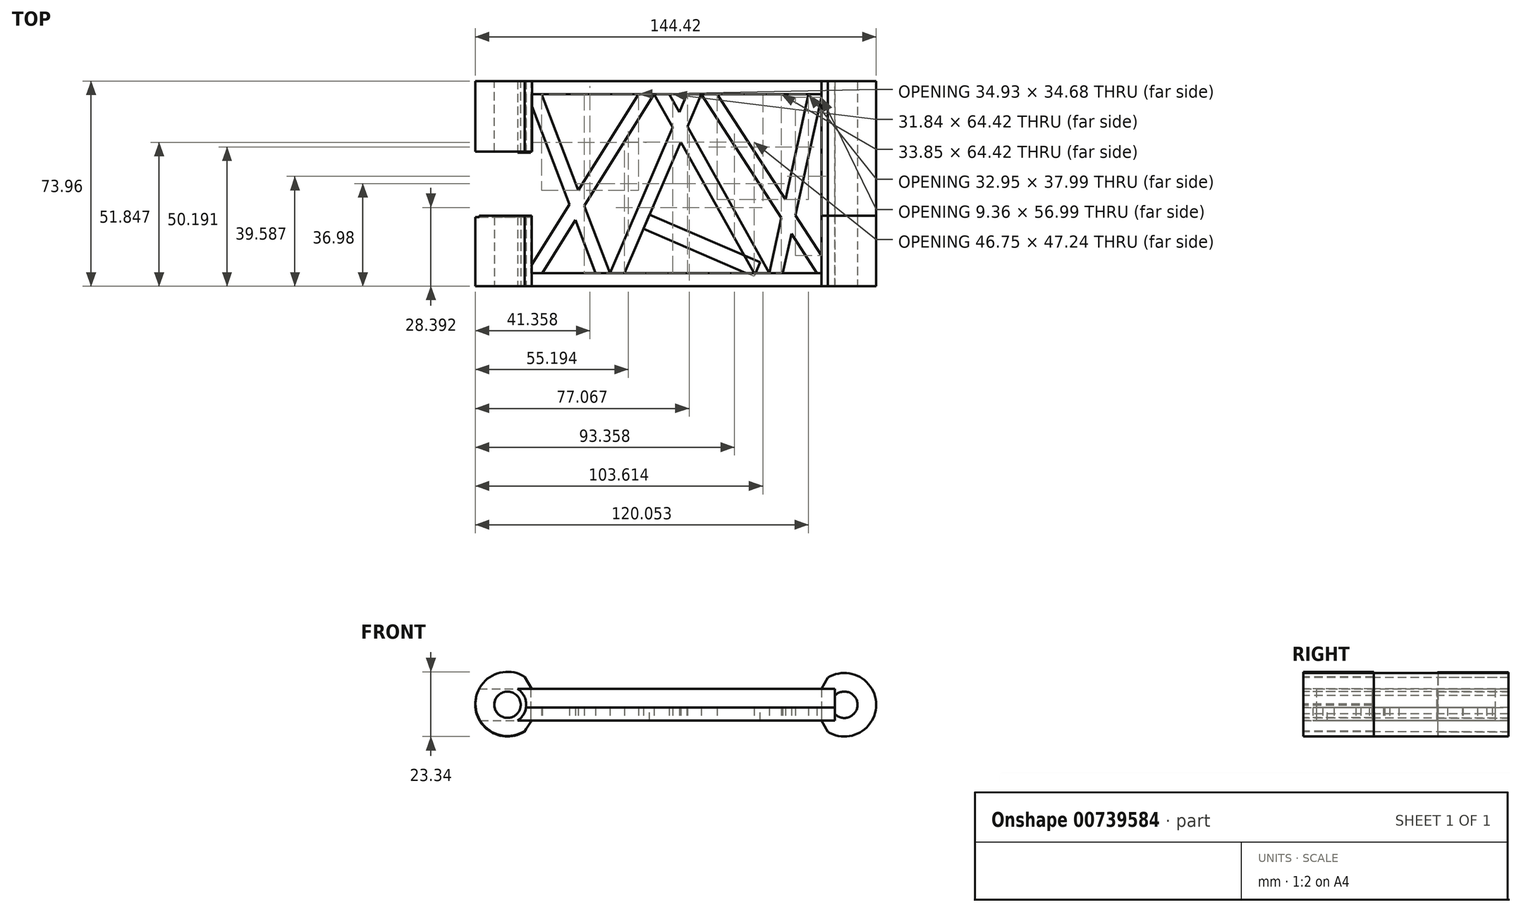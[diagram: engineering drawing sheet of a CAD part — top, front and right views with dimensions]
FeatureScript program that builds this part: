
annotation { "Feature Type Name" : "Feature", "Feature Type Description" : "" }
export const myFeature = defineFeature(function(context is Context, id is Id, definition is map)
    precondition{}
    {
        {
            var Q0;
            Q0=qCreatedBy(makeId("Top.planeOp"),FACE);
            var sketch = newSketch(context, id + "F0", { "sketchPlane" : qUnion([Q0])});
            skLineSegment(sketch, "E0", {"start": v(-109.82, 45.91) * mm, "end": v(-109.82, -28.05) * mm});
            skLineSegment(sketch, "E1", {"start": v(-109.82, -28.05) * mm, "end": v(4.48, -28.05) * mm});
            skLineSegment(sketch, "E2", {"start": v(4.48, -28.05) * mm, "end": v(4.48, 45.91) * mm});
            skLineSegment(sketch, "E3", {"start": v(4.48, 45.91) * mm, "end": v(-109.82, 45.91) * mm});
            skLineSegment(sketch, "E4.0", {"start": v(-105.05, 41.14) * mm, "end": v(-105.05, -23.28) * mm});
            skLineSegment(sketch, "E4.1", {"start": v(-0.3, 41.14) * mm, "end": v(-105.05, 41.14) * mm});
            skLineSegment(sketch, "E4.2", {"start": v(-0.3, -23.28) * mm, "end": v(-0.3, 41.14) * mm});
            skLineSegment(sketch, "E4.3", {"start": v(-105.05, -23.28) * mm, "end": v(-0.3, -23.28) * mm});
            skLineSegment(sketch, "E5", {"start": v(-42.79, -23.28) * mm, "end": v(-36.04, -23.28) * mm});
            skLineSegment(sketch, "E6", {"start": v(-10.41, 41.14) * mm, "end": v(-5.27, 41.14) * mm});
            skLineSegment(sketch, "E7", {"start": v(1.6, 41.14) * mm, "end": v(-0.3, 41.76) * mm});
            skLineSegment(sketch, "E8", {"start": v(-43.58, 41.14) * mm, "end": v(-37.89, 41.14) * mm});
            skLineSegment(sketch, "E9", {"start": v(-9.59, 41.14) * mm, "end": v(-0.3, 41.14) * mm});
            skLineSegment(sketch, "E10", {"start": v(-105.05, -20.98) * mm, "end": v(-66.2, 41.14) * mm});
            skLineSegment(sketch, "E11", {"start": v(-66.2, 41.14) * mm, "end": v(-60.57, 41.14) * mm});
            skLineSegment(sketch, "E12", {"start": v(-60.57, 41.14) * mm, "end": v(-100.85, -23.28) * mm});
            skLineSegment(sketch, "E13", {"start": v(-60.57, 41.14) * mm, "end": v(-24.59, -23.28) * mm});
            skLineSegment(sketch, "E14", {"start": v(-24.59, -23.28) * mm, "end": v(-19.12, -23.28) * mm});
            skLineSegment(sketch, "E15", {"start": v(-19.12, -23.28) * mm, "end": v(-55.1, 41.14) * mm});
            skLineSegment(sketch, "E16", {"start": v(-55.1, 41.14) * mm, "end": v(-60.57, 41.14) * mm});
            skLineSegment(sketch, "E17", {"start": v(-19.12, -23.28) * mm, "end": v(-4.94, 41.14) * mm});
            skLineSegment(sketch, "E18", {"start": v(-4.94, 41.14) * mm, "end": v(-0.3, 41.14) * mm});
            skLineSegment(sketch, "E19", {"start": v(-0.3, 41.14) * mm, "end": v(-0.3, 40.03) * mm});
            skLineSegment(sketch, "E20", {"start": v(-0.3, 40.03) * mm, "end": v(-14.23, -23.28) * mm});
            skLineSegment(sketch, "E21", {"start": v(-1.9, -23.28) * mm, "end": v(-43.58, 41.14) * mm});
            skLineSegment(sketch, "E22", {"start": v(-37.89, 41.14) * mm, "end": v(-0.3, -16.96) * mm});
            skLineSegment(sketch, "E23", {"start": v(-0.3, -16.96) * mm, "end": v(-0.3, -23.28) * mm});
            skLineSegment(sketch, "E24", {"start": v(-43.58, 41.14) * mm, "end": v(-71.34, -23.28) * mm});
            skLineSegment(sketch, "E25", {"start": v(-71.34, -23.28) * mm, "end": v(-76.54, -23.28) * mm});
            skLineSegment(sketch, "E26", {"start": v(-76.54, -23.28) * mm, "end": v(-48.78, 41.14) * mm});
            skLineSegment(sketch, "E27", {"start": v(-48.78, 41.14) * mm, "end": v(-43.58, 41.14) * mm});
            skLineSegment(sketch, "E28", {"start": v(-76.54, -23.28) * mm, "end": v(-101.14, 41.14) * mm});
            skLineSegment(sketch, "E29", {"start": v(-101.14, 41.14) * mm, "end": v(-105.05, 41.14) * mm});
            skLineSegment(sketch, "E30", {"start": v(-105.05, 37.99) * mm, "end": v(-81.65, -23.28) * mm});
            skLineSegment(sketch, "E31", {"start": v(-81.65, -23.28) * mm, "end": v(-76.54, -23.28) * mm});
            skSolve(sketch);
        }
        {
            var Q0;
            {var subQ5=sQuery(id+"F0.wireOp",EDGE,"E4.0");var subQ7=sQuery(id+"F0.wireOp",EDGE,"E30");var subQ8=makeQuery(id+"F0.imprint","INTERSECT",VERTEX,{"derivedFrom":[subQ5,subQ7]});Q0=makeQuery(id+"F0.imprint","IMPRINT",FACE,{"disambiguationData":[TD([[makeQuery(id+"F0.imprint","IMPRINT",EDGE,{"disambiguationData":[TD([[subQ8,1.0]])],"derivedFrom":subQ5}),1.0]])]});}
            var Q1;
            {var subQ3=sQuery(id+"F0.wireOp",EDGE,"E4.3");var subQ6=sQuery(id+"F0.wireOp",EDGE,"E4.0");var subQ9=makeQuery(id+"F0.imprint","INTERSECT",VERTEX,{"derivedFrom":[subQ6,subQ3]});Q1=makeQuery(id+"F0.imprint","IMPRINT",FACE,{"disambiguationData":[TD([[makeQuery(id+"F0.imprint","IMPRINT",EDGE,{"disambiguationData":[TD([[subQ9,1.0]])],"derivedFrom":subQ6}),1.0]])]});}
            var Q2;
            {var subQ0=sQuery(id+"F0.wireOp",EDGE,"E28");var subQ1=sQuery(id+"F0.wireOp",EDGE,"E10");var subQ2=makeQuery(id+"F0.imprint","INTERSECT",VERTEX,{"derivedFrom":[subQ1,subQ0]});Q2=makeQuery(id+"F0.imprint","IMPRINT",FACE,{"disambiguationData":[TD([[makeQuery(id+"F0.imprint","IMPRINT",EDGE,{"disambiguationData":[TD([[subQ2,1.0]])],"derivedFrom":subQ1}),-1.0]])]});}
            var Q3;
            {var subQ3=sQuery(id+"F0.wireOp",EDGE,"E30");var subQ5=sQuery(id+"F0.wireOp",EDGE,"E12");var subQ7=makeQuery(id+"F0.imprint","INTERSECT",VERTEX,{"derivedFrom":[subQ5,subQ3]});Q3=makeQuery(id+"F0.imprint","IMPRINT",FACE,{"disambiguationData":[TD([[makeQuery(id+"F0.imprint","IMPRINT",EDGE,{"disambiguationData":[TD([[subQ7,1.0]])],"derivedFrom":subQ5}),1.0]])]});}
            var Q4;
            {var subQ0=sQuery(id+"F0.wireOp",EDGE,"E10");var subQ1=sQuery(id+"F0.wireOp",EDGE,"E4.1");var subQ2=makeQuery(id+"F0.imprint","INTERSECT",VERTEX,{"derivedFrom":[subQ1,subQ0]});Q4=makeQuery(id+"F0.imprint","IMPRINT",FACE,{"disambiguationData":[TD([[makeQuery(id+"F0.imprint","IMPRINT",EDGE,{"disambiguationData":[TD([[subQ2,1.0]])],"derivedFrom":subQ0}),-1.0]])]});}
            var Q5;
            Q5=makeQuery(id+"F0.imprint","IMPRINT",FACE,{"disambiguationData":[TD([[makeQuery(id+"F0.imprint","IMPRINT",EDGE,{"derivedFrom":sQuery(id+"F0.wireOp",EDGE,"E0")}),1.0]])]});
            var Q6;
            {var subQ0=sQuery(id+"F0.wireOp",EDGE,"E24");var subQ5=sQuery(id+"F0.wireOp",EDGE,"E13");var subQ6=makeQuery(id+"F0.imprint","INTERSECT",VERTEX,{"derivedFrom":[subQ5,subQ0]});Q6=makeQuery(id+"F0.imprint","IMPRINT",FACE,{"disambiguationData":[TD([[makeQuery(id+"F0.imprint","IMPRINT",EDGE,{"disambiguationData":[TD([[subQ6,1.0]])],"derivedFrom":subQ5}),-1.0]])]});}
            var Q7;
            {var subQ0=sQuery(id+"F0.wireOp",EDGE,"E24");var subQ1=sQuery(id+"F0.wireOp",EDGE,"E13");var subQ2=makeQuery(id+"F0.imprint","INTERSECT",VERTEX,{"derivedFrom":[subQ1,subQ0]});Q7=makeQuery(id+"F0.imprint","IMPRINT",FACE,{"disambiguationData":[TD([[makeQuery(id+"F0.imprint","IMPRINT",EDGE,{"disambiguationData":[TD([[subQ2,1.0]])],"derivedFrom":subQ1}),1.0]])]});}
            var Q8;
            {var subQ3=sQuery(id+"F0.wireOp",EDGE,"E13");var subQ5=sQuery(id+"F0.wireOp",EDGE,"E24");var subQ7=makeQuery(id+"F0.imprint","INTERSECT",VERTEX,{"derivedFrom":[subQ3,subQ5]});Q8=makeQuery(id+"F0.imprint","IMPRINT",FACE,{"disambiguationData":[TD([[makeQuery(id+"F0.imprint","IMPRINT",EDGE,{"disambiguationData":[TD([[subQ7,-1.0]])],"derivedFrom":subQ3}),1.0]])]});}
            var Q9;
            {var subQ0=sQuery(id+"F0.wireOp",EDGE,"E26");var subQ5=sQuery(id+"F0.wireOp",EDGE,"E15");var subQ7=makeQuery(id+"F0.imprint","INTERSECT",VERTEX,{"derivedFrom":[subQ5,subQ0]});Q9=makeQuery(id+"F0.imprint","IMPRINT",FACE,{"disambiguationData":[TD([[makeQuery(id+"F0.imprint","IMPRINT",EDGE,{"disambiguationData":[TD([[subQ7,1.0]])],"derivedFrom":subQ5}),-1.0]])]});}
            var Q10;
            {var subQ3=sQuery(id+"F0.wireOp",EDGE,"E15");var subQ5=sQuery(id+"F0.wireOp",EDGE,"E26");var subQ6=makeQuery(id+"F0.imprint","INTERSECT",VERTEX,{"derivedFrom":[subQ3,subQ5]});Q10=makeQuery(id+"F0.imprint","IMPRINT",FACE,{"disambiguationData":[TD([[makeQuery(id+"F0.imprint","IMPRINT",EDGE,{"disambiguationData":[TD([[subQ6,-1.0]])],"derivedFrom":subQ3}),1.0]])]});}
            var Q11;
            {var subQ0=sQuery(id+"F0.wireOp",EDGE,"E22");var subQ5=sQuery(id+"F0.wireOp",EDGE,"E17");var subQ6=makeQuery(id+"F0.imprint","INTERSECT",VERTEX,{"derivedFrom":[subQ5,subQ0]});Q11=makeQuery(id+"F0.imprint","IMPRINT",FACE,{"disambiguationData":[TD([[makeQuery(id+"F0.imprint","IMPRINT",EDGE,{"disambiguationData":[TD([[subQ6,1.0]])],"derivedFrom":subQ5}),1.0]])]});}
            var Q12;
            {var subQ0=sQuery(id+"F0.wireOp",EDGE,"E22");var subQ1=sQuery(id+"F0.wireOp",EDGE,"E17");var subQ2=makeQuery(id+"F0.imprint","INTERSECT",VERTEX,{"derivedFrom":[subQ1,subQ0]});Q12=makeQuery(id+"F0.imprint","IMPRINT",FACE,{"disambiguationData":[TD([[makeQuery(id+"F0.imprint","IMPRINT",EDGE,{"disambiguationData":[TD([[subQ2,1.0]])],"derivedFrom":subQ1}),-1.0]])]});}
            var Q13;
            {var subQ3=sQuery(id+"F0.wireOp",EDGE,"E20");var subQ5=sQuery(id+"F0.wireOp",EDGE,"E21");var subQ7=makeQuery(id+"F0.imprint","INTERSECT",VERTEX,{"derivedFrom":[subQ3,subQ5]});Q13=makeQuery(id+"F0.imprint","IMPRINT",FACE,{"disambiguationData":[TD([[makeQuery(id+"F0.imprint","IMPRINT",EDGE,{"disambiguationData":[TD([[subQ7,-1.0]])],"derivedFrom":subQ3}),-1.0]])]});}
            var Q14;
            {var subQ5=sQuery(id+"F0.wireOp",EDGE,"E4.2");var subQ7=sQuery(id+"F0.wireOp",EDGE,"E22");var subQ9=makeQuery(id+"F0.imprint","INTERSECT",VERTEX,{"derivedFrom":[subQ5,subQ7]});Q14=makeQuery(id+"F0.imprint","IMPRINT",FACE,{"disambiguationData":[TD([[makeQuery(id+"F0.imprint","IMPRINT",EDGE,{"disambiguationData":[TD([[subQ9,1.0]])],"derivedFrom":subQ5}),1.0]])]});}
            var Q15;
            {var subQ1=sQuery(id+"F0.wireOp",EDGE,"E4.2");var subQ7=sQuery(id+"F0.wireOp",EDGE,"E4.1");var subQ9=makeQuery(id+"F0.imprint","INTERSECT",VERTEX,{"derivedFrom":[subQ7,subQ1]});Q15=makeQuery(id+"F0.imprint","IMPRINT",FACE,{"disambiguationData":[TD([[makeQuery(id+"F0.imprint","IMPRINT",EDGE,{"disambiguationData":[TD([[subQ9,-1.0]])],"derivedFrom":subQ7}),1.0]])]});}
            extrude(context, id + "F1", {"entities" : qUnion([Q0, Q1, Q2, Q3, Q4, Q5, Q6, Q7, Q8, Q9, Q10, Q11, Q12, Q13, Q14, Q15]), "depth" : 4.78 * mm, "offsetDistance" : 25.4 * mm});
        }
        {
            var Q0;
            Q0=makeQuery(id+"F0.imprint","IMPRINT",FACE,{"disambiguationData":[TD([[makeQuery(id+"F0.imprint","IMPRINT",EDGE,{"derivedFrom":sQuery(id+"F0.wireOp",EDGE,"E0")}),1.0]])]});
            extrude(context, id + "F2", {"entities" : qUnion([Q0]), "depth" : 11.43 * mm, "offsetDistance" : 25.4 * mm});
        }
        {
            var Q0;
            Q0=makeQuery(id+"F2.opExtrude","SWEPT_FACE",FACE,{"disambiguationData":[OSD([sQuery(id+"F0.wireOp",EDGE,"E1")])]});
            var sketch = newSketch(context, id + "F3", { "sketchPlane" : qUnion([Q0])});
            skArc(sketch, "E32", {"start": v(-109.82, 11.43) * mm, "mid": v(-120.12, 5.71) * mm, "end": v(-109.82, 0) * mm});
            skArc(sketch, "E33.0", {"start": v(-107.3, 15.48) * mm, "mid": v(-124.9, 5.72) * mm, "end": v(-107.3, -4.05) * mm});
            skLineSegment(sketch, "E34", {"start": v(-107.3, 15.48) * mm, "end": v(-104.75, 11.43) * mm});
            skLineSegment(sketch, "E35", {"start": v(-107.3, -4.05) * mm, "end": v(-104.75, 0) * mm});
            skCircle(sketch, "E36", {"center": v(-113.39, 5.72) * mm, "radius": 6.74 * mm});
            skSolve(sketch);
        }
        {
            var Q0;
            Q0=sQuery(id+"F3.wireOp",VERTEX,"E32.center");
            var Q1;
            Q1=makeQuery(id+"F1.opExtrude","SWEPT_BODY",BODY,{"disambiguationData":[OSD([sQuery(id+"F0.wireOp",EDGE,"E0"),sQuery(id+"F0.wireOp",EDGE,"E1"),sQuery(id+"F0.wireOp",EDGE,"E2"),sQuery(id+"F0.wireOp",EDGE,"E3"),sQuery(id+"F0.wireOp",EDGE,"E4.0"),sQuery(id+"F0.wireOp",EDGE,"E4.1"),sQuery(id+"F0.wireOp",EDGE,"E4.2"),sQuery(id+"F0.wireOp",EDGE,"E4.3"),sQuery(id+"F0.wireOp",EDGE,"E10"),sQuery(id+"F0.wireOp",EDGE,"E12"),sQuery(id+"F0.wireOp",EDGE,"E13"),sQuery(id+"F0.wireOp",EDGE,"E15"),sQuery(id+"F0.wireOp",EDGE,"E17"),sQuery(id+"F0.wireOp",EDGE,"E20"),sQuery(id+"F0.wireOp",EDGE,"E21"),sQuery(id+"F0.wireOp",EDGE,"E22"),sQuery(id+"F0.wireOp",EDGE,"E24"),sQuery(id+"F0.wireOp",EDGE,"E26"),sQuery(id+"F0.wireOp",EDGE,"E28"),sQuery(id+"F0.wireOp",EDGE,"E30")])]});
            var Q2;
            Q2=makeQuery(id+"F2.opExtrude","SWEPT_BODY",BODY,{"disambiguationData":[OSD([sQuery(id+"F0.wireOp",EDGE,"E0"),sQuery(id+"F0.wireOp",EDGE,"E1"),sQuery(id+"F0.wireOp",EDGE,"E2"),sQuery(id+"F0.wireOp",EDGE,"E3"),sQuery(id+"F0.wireOp",EDGE,"E4.0"),sQuery(id+"F0.wireOp",EDGE,"E4.1"),sQuery(id+"F0.wireOp",EDGE,"E4.2"),sQuery(id+"F0.wireOp",EDGE,"E4.3")])]});
            hole(context, id + "F4", {"style" : HoleStyle.SIMPLE, "endStyle" : HoleEndStyle.THROUGH, "holeDiameter" : 13.46 * mm, "majorDiameter" : 6.35 * mm, "isTappedThrough" : true, "tappedDepth" : 12.7 * mm, "tapClearance" : 3, "locations" : qUnion([Q0]), "scope" : qUnion([Q1, Q2])});
        }
        {
            var Q0;
            Q0=makeQuery(id+"F2.opExtrude","SWEPT_FACE",FACE,{"disambiguationData":[OSD([sQuery(id+"F0.wireOp",EDGE,"E3")])]});
            var sketch = newSketch(context, id + "F5", { "sketchPlane" : qUnion([Q0])});
            skCircle(sketch, "E37", {"center": v(113.39, 5.72) * mm, "radius": 4.76 * mm});
            skArc(sketch, "E38", {"start": v(107.35, -3.99) * mm, "mid": v(125.03, 5.93) * mm, "end": v(107.26, 15.7) * mm});
            skLineSegment(sketch, "E39", {"start": v(107.26, 15.7) * mm, "end": v(104.6, 11.43) * mm});
            skLineSegment(sketch, "E40", {"start": v(107.35, -3.99) * mm, "end": v(104.83, 0) * mm});
            skSolve(sketch);
        }
        {
            var Q0;
            Q0=makeQuery(id+"F5.imprint","IMPRINT",FACE,{"disambiguationData":[TD([[makeQuery(id+"F5.imprint","IMPRINT",EDGE,{"derivedFrom":sQuery(id+"F5.wireOp",EDGE,"E37")}),-1.0]])]});
            extrude(context, id + "F6", {"entities" : qUnion([Q0]), "oppositeDirection" : true, "depth" : 25.4 * mm, "offsetDistance" : 25.4 * mm});
        }
        {
            var Q0;
            Q0=makeQuery(id+"F2.opExtrude","SWEPT_FACE",FACE,{"disambiguationData":[OSD([sQuery(id+"F0.wireOp",EDGE,"E1")])]});
            var sketch = newSketch(context, id + "F7", { "sketchPlane" : qUnion([Q0])});
            skArc(sketch, "E41.0", {"start": v(2, -4.09) * mm, "mid": v(19.4, 5.71) * mm, "end": v(2, 15.52) * mm});
            skCircle(sketch, "E42", {"center": v(7.94, 5.72) * mm, "radius": 4.76 * mm});
            skLineSegment(sketch, "E43", {"start": v(2, 15.52) * mm, "end": v(-0.3, 11.43) * mm});
            skLineSegment(sketch, "E44", {"start": v(2, -4.09) * mm, "end": v(-0.3, 0) * mm});
            skArc(sketch, "E45", {"start": v(-107.2, 15.8) * mm, "mid": v(-124.97, 6.07) * mm, "end": v(-107.26, -3.78) * mm});
            skLineSegment(sketch, "E46", {"start": v(-107.2, 15.8) * mm, "end": v(-104.65, 11.43) * mm});
            skLineSegment(sketch, "E47", {"start": v(-107.26, -3.78) * mm, "end": v(-104.65, 0) * mm});
            skLineSegment(sketch, "E48", {"start": v(-104.65, 0) * mm, "end": v(-104.65, 11.43) * mm});
            skArc(sketch, "E49", {"start": v(-108.66, 6.03) * mm, "mid": v(-113.69, 10.45) * mm, "end": v(-118.17, 5.48) * mm});
            skArc(sketch, "E50", {"start": v(-118.17, 5.48) * mm, "mid": v(-113.14, 1) * mm, "end": v(-108.66, 6.03) * mm});
            skSolve(sketch);
        }
        {
            var Q0;
            {var subQ0=sQuery(id+"F7.wireOp",EDGE,"xlH9iZdu-T5Ql-fwjw-VsTz-vYfNJ1fnH3hM");Q0=makeQuery(id+"F7.imprint","IMPRINT",FACE,{"disambiguationData":[TD([[makeQuery(id+"F7.imprint","IMPRINT",EDGE,{"derivedFrom":subQ0}),-1.0]])]});}
            var Q1;
            Q1=makeQuery(id+"F7.imprint","IMPRINT",FACE,{"disambiguationData":[TD([[makeQuery(id+"F7.imprint","IMPRINT",EDGE,{"derivedFrom":sQuery(id+"F7.wireOp",EDGE,"E41.0")}),1.0]])]});
            var Q2;
            Q2=makeQuery(id+"F7.imprint","IMPRINT",FACE,{"disambiguationData":[TD([[makeQuery(id+"F7.imprint","IMPRINT",EDGE,{"derivedFrom":sQuery(id+"F7.wireOp",EDGE,"E45")}),1.0]])]});
            extrude(context, id + "F8", {"entities" : qUnion([Q0, Q1, Q2]), "oppositeDirection" : true, "depth" : 25.4 * mm, "offsetDistance" : 25.4 * mm});
        }
        {
            var Q0;
            Q0=makeQuery(id+"F2.opExtrude","SWEPT_FACE",FACE,{"disambiguationData":[OSD([sQuery(id+"F0.wireOp",EDGE,"E4.0")])]});
            var sketch = newSketch(context, id + "F9", { "sketchPlane" : qUnion([Q0])});
            skLineSegment(sketch, "E51", {"start": v(-3.12, 11.43) * mm, "end": v(-3.12, 0) * mm});
            skLineSegment(sketch, "E52", {"start": v(20.14, 11.43) * mm, "end": v(20.14, 0) * mm});
            skSolve(sketch);
        }
        {
            var Q0;
            {var subQ0=sQuery(id+"F9.wireOp",EDGE,"E51");Q0=makeQuery(id+"F9.imprint","IMPRINT",FACE,{"disambiguationData":[TD([[makeQuery(id+"F9.imprint","IMPRINT",EDGE,{"derivedFrom":subQ0}),1.0]])]});}
            extrude(context, id + "F10", {"entities" : qUnion([Q0]), "operationType" : NewBodyOperationType.REMOVE, "oppositeDirection" : true, "depth" : 25.4 * mm, "offsetDistance" : 25.4 * mm});
        }
        {
            var Q0;
            {var subQ0=sQuery(id+"F0.wireOp",EDGE,"E24");Q0=makeQuery(id+"F1.opExtrude","SWEPT_FACE",FACE,{"disambiguationData":[OSD([subQ0]),TDD([makeQuery(id+"F0.imprint","IMPRINT",EDGE,{"disambiguationData":[TD([[makeQuery(id+"F0.imprint","INTERSECT",VERTEX,{"derivedFrom":[sQuery(id+"F0.wireOp",EDGE,"E4.3"),subQ0]}),1.0]])],"derivedFrom":subQ0})])]});}
            var sketch = newSketch(context, id + "F11", { "sketchPlane" : qUnion([Q0])});
            skLineSegment(sketch, "E53", {"start": v(-32.24, 4.78) * mm, "end": v(-32.24, 0) * mm});
            skLineSegment(sketch, "E54", {"start": v(-32.24, 0) * mm, "end": v(-26.68, 0) * mm});
            skLineSegment(sketch, "E55", {"start": v(-26.68, 0) * mm, "end": v(-26.68, 4.78) * mm});
            skLineSegment(sketch, "E56", {"start": v(-26.68, 4.78) * mm, "end": v(-32.24, 4.78) * mm});
            skSolve(sketch);
        }
        {
            var Q0;
            Q0 = qSketchRegion(id + "F11", true);
            extrude(context, id + "F12", {"entities" : qUnion([Q0]), "depth" : 43.43 * mm, "offsetDistance" : 25.4 * mm});
        }
        {
            var Q0;
            Q0=makeQuery(id+"F8.opExtrude","CAP_FACE",FACE,{"disambiguationData":[OSD([sQuery(id+"F0.wireOp",EDGE,"E1"),sQuery(id+"F0.wireOp",EDGE,"E2"),sQuery(id+"F7.wireOp",EDGE,"E41.0"),sQuery(id+"F7.wireOp",EDGE,"E42"),sQuery(id+"F7.wireOp",EDGE,"E43"),sQuery(id+"F7.wireOp",EDGE,"E44")])],"isStart":false});
            extrude(context, id + "F13", {"entities" : qUnion([Q0]), "depth" : 48.5 * mm, "offsetDistance" : 25.4 * mm});
        }
    });
